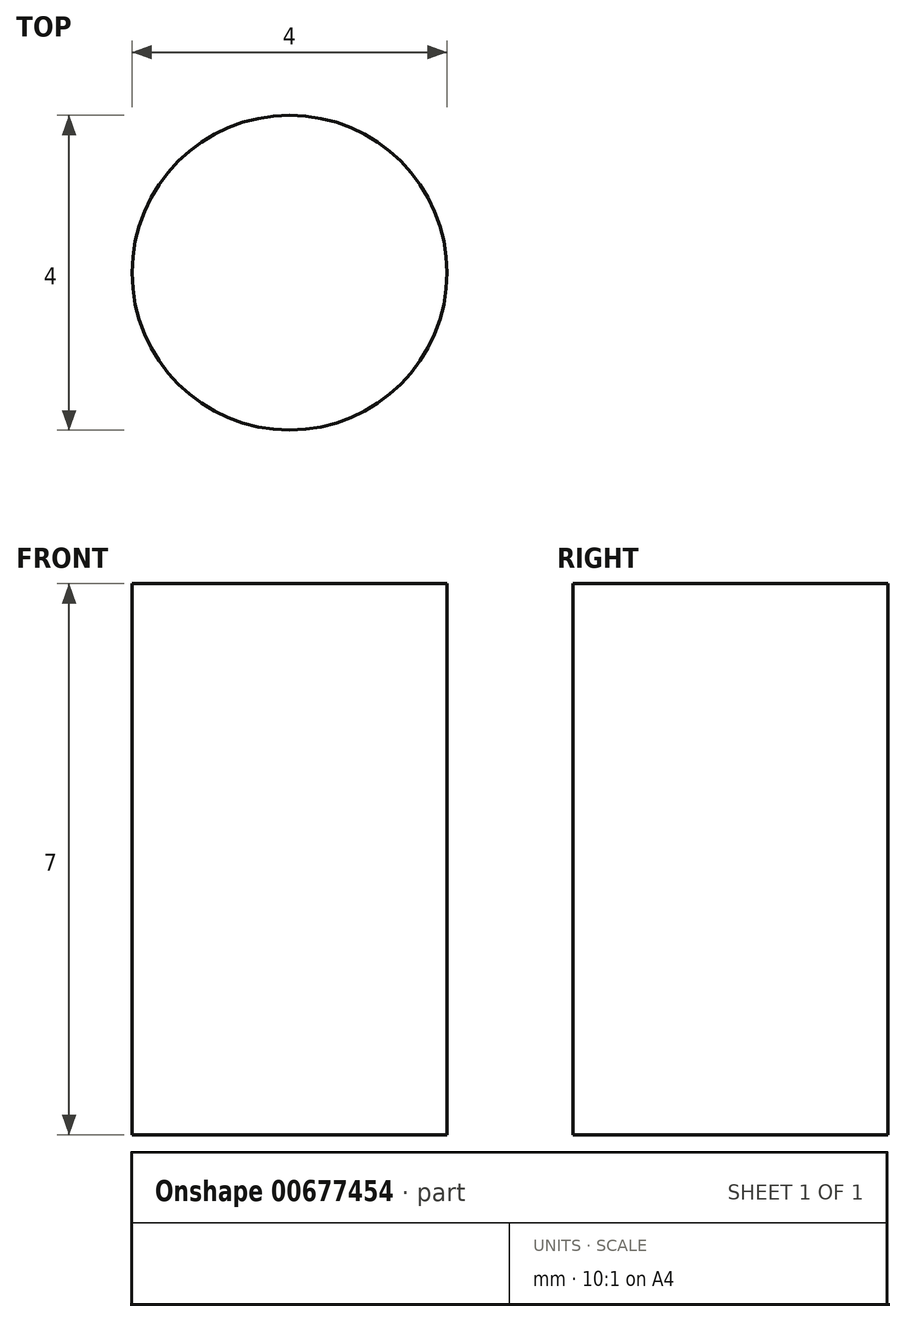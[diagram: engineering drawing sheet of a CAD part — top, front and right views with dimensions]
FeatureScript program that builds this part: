
annotation { "Feature Type Name" : "Feature", "Feature Type Description" : "" }
export const myFeature = defineFeature(function(context is Context, id is Id, definition is map)
    precondition{}
    {
        {
            var Q0;
            Q0=qCreatedBy(makeId("Top.planeOp"),FACE);
            var sketch = newSketch(context, id + "F0", { "sketchPlane" : qUnion([Q0])});
            skCircle(sketch, "E0", {"center": v(0, 0) * mm, "radius": 2 * mm});
            skSolve(sketch);
        }
        {
            var Q0;
            Q0 = qSketchRegion(id + "F0", true);
            extrude(context, id + "F1", {"entities" : qUnion([Q0]), "depth" : 7 * mm, "offsetDistance" : 25 * mm});
        }
    });
